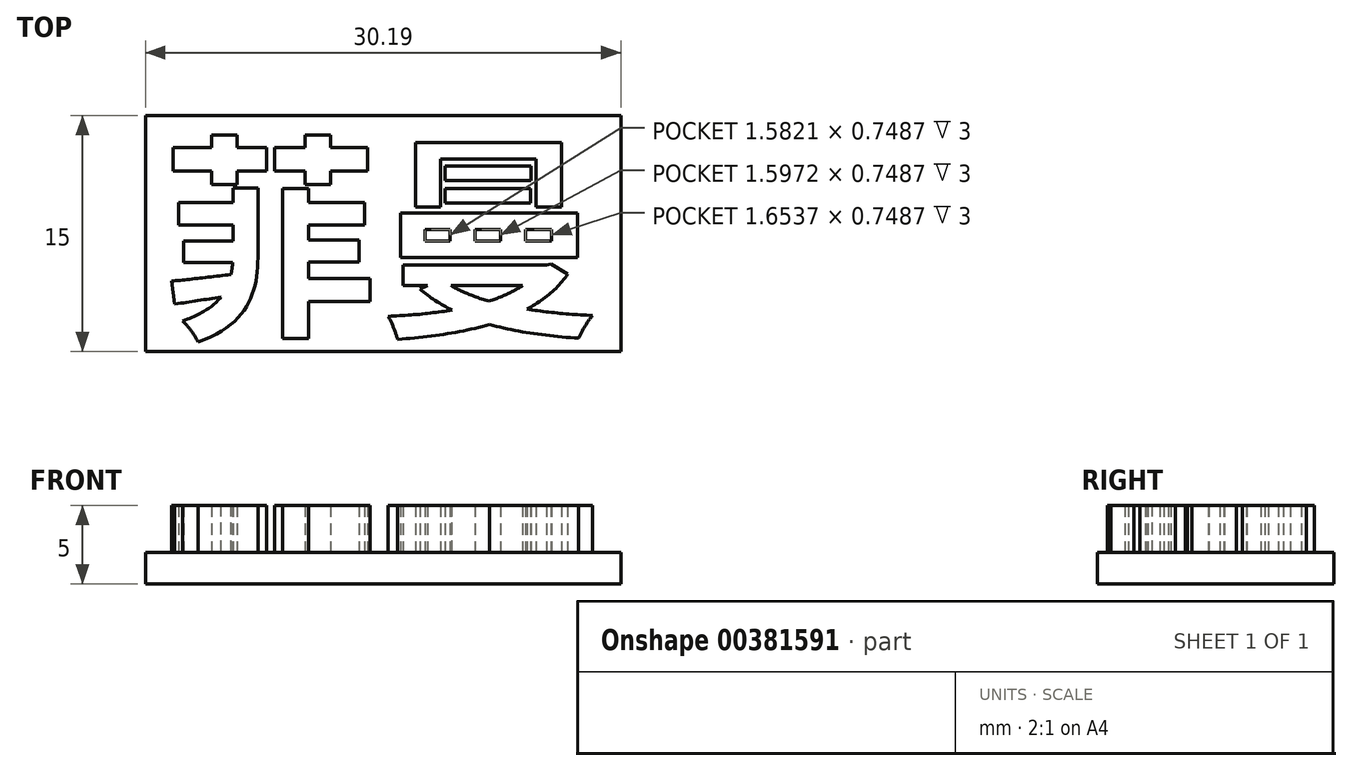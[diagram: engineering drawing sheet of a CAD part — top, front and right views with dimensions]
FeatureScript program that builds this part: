
annotation { "Feature Type Name" : "Feature", "Feature Type Description" : "" }
export const myFeature = defineFeature(function(context is Context, id is Id, definition is map)
    precondition{}
    {
        {
            var Q0;
            Q0=qCreatedBy(makeId("Top.planeOp"),FACE);
            var sketch = newSketch(context, id + "F0", { "sketchPlane" : qUnion([Q0])});
            skText(sketch, "E0", { "text": "菲曼", "fontName": "NotoSansCJKtc-Bold.otf"});
            skLineSegment(sketch, "E1.bottom", {"start": v(-1, 13) * mm, "end": v(29.2, 13) * mm});
            skLineSegment(sketch, "E1.top", {"start": v(-1, -2) * mm, "end": v(29.2, -2) * mm});
            skLineSegment(sketch, "E1.left", {"start": v(-1, 13) * mm, "end": v(-1, -2) * mm});
            skLineSegment(sketch, "E1.right", {"start": v(29.2, 13) * mm, "end": v(29.2, -2) * mm});
            const initialGuessF0  = {"E0": [0, 0, 1, 0, 0.01]};
            skSetInitialGuess(sketch, initialGuessF0);
            skSolve(sketch);
        }
        {
            var Q0;
            Q0=makeQuery(id+"F0.imprint","IMPRINT",FACE,{"disambiguationData":[TD([[makeQuery(id+"F0.imprint","IMPRINT",EDGE,{"derivedFrom":sQuery(id+"F0.wireOp",EDGE,"E0.sketch_text.stroke-0")}),-1.0]])]});
            var Q1;
            Q1=makeQuery(id+"F0.imprint","IMPRINT",FACE,{"disambiguationData":[TD([[makeQuery(id+"F0.imprint","IMPRINT",EDGE,{"derivedFrom":sQuery(id+"F0.wireOp",EDGE,"E0.sketch_text.stroke-0")}),1.0]])]});
            var Q2;
            Q2=makeQuery(id+"F0.imprint","IMPRINT",FACE,{"disambiguationData":[TD([[makeQuery(id+"F0.imprint","IMPRINT",EDGE,{"derivedFrom":sQuery(id+"F0.wireOp",EDGE,"E0.sketch_text.stroke-19")}),1.0]])]});
            var Q3;
            Q3=makeQuery(id+"F0.imprint","IMPRINT",FACE,{"disambiguationData":[TD([[makeQuery(id+"F0.imprint","IMPRINT",EDGE,{"derivedFrom":sQuery(id+"F0.wireOp",EDGE,"E0.sketch_text.stroke-45")}),1.0]])]});
            var Q4;
            Q4=makeQuery(id+"F0.imprint","IMPRINT",FACE,{"disambiguationData":[TD([[makeQuery(id+"F0.imprint","IMPRINT",EDGE,{"derivedFrom":sQuery(id+"F0.wireOp",EDGE,"E0.sketch_text.stroke-41")}),1.0]])]});
            var Q5;
            Q5=makeQuery(id+"F0.imprint","IMPRINT",FACE,{"disambiguationData":[TD([[makeQuery(id+"F0.imprint","IMPRINT",EDGE,{"derivedFrom":sQuery(id+"F0.wireOp",EDGE,"E0.sketch_text.stroke-37")}),1.0]])]});
            var Q6;
            Q6=makeQuery(id+"F0.imprint","IMPRINT",FACE,{"disambiguationData":[TD([[makeQuery(id+"F0.imprint","IMPRINT",EDGE,{"derivedFrom":sQuery(id+"F0.wireOp",EDGE,"E0.sketch_text.stroke-69")}),1.0]])]});
            var Q7;
            Q7=makeQuery(id+"F0.imprint","IMPRINT",FACE,{"disambiguationData":[TD([[makeQuery(id+"F0.imprint","IMPRINT",EDGE,{"derivedFrom":sQuery(id+"F0.wireOp",EDGE,"E0.sketch_text.stroke-69")}),-1.0]])]});
            var Q8;
            Q8=makeQuery(id+"F0.imprint","IMPRINT",FACE,{"disambiguationData":[TD([[makeQuery(id+"F0.imprint","IMPRINT",EDGE,{"derivedFrom":sQuery(id+"F0.wireOp",EDGE,"E0.sketch_text.stroke-49")}),1.0]])]});
            var Q9;
            Q9=makeQuery(id+"F0.imprint","IMPRINT",FACE,{"disambiguationData":[TD([[makeQuery(id+"F0.imprint","IMPRINT",EDGE,{"derivedFrom":sQuery(id+"F0.wireOp",EDGE,"E0.sketch_text.stroke-85")}),1.0]])]});
            var Q10;
            Q10=makeQuery(id+"F0.imprint","IMPRINT",FACE,{"disambiguationData":[TD([[makeQuery(id+"F0.imprint","IMPRINT",EDGE,{"derivedFrom":sQuery(id+"F0.wireOp",EDGE,"E0.sketch_text.stroke-85")}),-1.0]])]});
            var Q11;
            Q11=makeQuery(id+"F0.imprint","IMPRINT",FACE,{"disambiguationData":[TD([[makeQuery(id+"F0.imprint","IMPRINT",EDGE,{"derivedFrom":sQuery(id+"F0.wireOp",EDGE,"E0.sketch_text.stroke-138")}),1.0]])]});
            var Q12;
            Q12=makeQuery(id+"F0.imprint","IMPRINT",FACE,{"disambiguationData":[TD([[makeQuery(id+"F0.imprint","IMPRINT",EDGE,{"derivedFrom":sQuery(id+"F0.wireOp",EDGE,"E0.sketch_text.stroke-142")}),1.0]])]});
            var Q13;
            Q13=makeQuery(id+"F0.imprint","IMPRINT",FACE,{"disambiguationData":[TD([[makeQuery(id+"F0.imprint","IMPRINT",EDGE,{"derivedFrom":sQuery(id+"F0.wireOp",EDGE,"E0.sketch_text.stroke-57")}),1.0]])]});
            var Q14;
            Q14=makeQuery(id+"F0.imprint","IMPRINT",FACE,{"disambiguationData":[TD([[makeQuery(id+"F0.imprint","IMPRINT",EDGE,{"derivedFrom":sQuery(id+"F0.wireOp",EDGE,"E0.sketch_text.stroke-65")}),1.0]])]});
            var Q15;
            Q15=makeQuery(id+"F0.imprint","IMPRINT",FACE,{"disambiguationData":[TD([[makeQuery(id+"F0.imprint","IMPRINT",EDGE,{"derivedFrom":sQuery(id+"F0.wireOp",EDGE,"E0.sketch_text.stroke-81")}),-1.0]])]});
            var Q16;
            Q16=makeQuery(id+"F0.imprint","IMPRINT",FACE,{"disambiguationData":[TD([[makeQuery(id+"F0.imprint","IMPRINT",EDGE,{"derivedFrom":sQuery(id+"F0.wireOp",EDGE,"E0.sketch_text.stroke-77")}),-1.0]])]});
            var Q17;
            Q17=makeQuery(id+"F0.imprint","IMPRINT",FACE,{"disambiguationData":[TD([[makeQuery(id+"F0.imprint","IMPRINT",EDGE,{"derivedFrom":sQuery(id+"F0.wireOp",EDGE,"E0.sketch_text.stroke-73")}),-1.0]])]});
            var Q18;
            Q18=makeQuery(id+"F0.imprint","IMPRINT",FACE,{"disambiguationData":[TD([[makeQuery(id+"F0.imprint","IMPRINT",EDGE,{"derivedFrom":sQuery(id+"F0.wireOp",EDGE,"E0.sketch_text.stroke-89")}),1.0]])]});
            var Q19;
            Q19=makeQuery(id+"F0.imprint","IMPRINT",FACE,{"disambiguationData":[TD([[makeQuery(id+"F0.imprint","IMPRINT",EDGE,{"derivedFrom":sQuery(id+"F0.wireOp",EDGE,"E0.sketch_text.stroke-89")}),-1.0]])]});
            extrude(context, id + "F1", {"entities" : qUnion([Q0, Q1, Q2, Q3, Q4, Q5, Q6, Q7, Q8, Q9, Q10, Q11, Q12, Q13, Q14, Q15, Q16, Q17, Q18, Q19]), "oppositeDirection" : true, "depth" : 2 * mm, "offsetDistance" : 25 * mm});
        }
        {
            var Q0;
            Q0=makeQuery(id+"F0.imprint","IMPRINT",FACE,{"disambiguationData":[TD([[makeQuery(id+"F0.imprint","IMPRINT",EDGE,{"derivedFrom":sQuery(id+"F0.wireOp",EDGE,"E0.sketch_text.stroke-0")}),1.0]])]});
            var Q1;
            Q1=makeQuery(id+"F0.imprint","IMPRINT",FACE,{"disambiguationData":[TD([[makeQuery(id+"F0.imprint","IMPRINT",EDGE,{"derivedFrom":sQuery(id+"F0.wireOp",EDGE,"E0.sketch_text.stroke-19")}),1.0]])]});
            var Q2;
            Q2=makeQuery(id+"F0.imprint","IMPRINT",FACE,{"disambiguationData":[TD([[makeQuery(id+"F0.imprint","IMPRINT",EDGE,{"derivedFrom":sQuery(id+"F0.wireOp",EDGE,"E0.sketch_text.stroke-69")}),1.0]])]});
            var Q3;
            Q3=makeQuery(id+"F0.imprint","IMPRINT",FACE,{"disambiguationData":[TD([[makeQuery(id+"F0.imprint","IMPRINT",EDGE,{"derivedFrom":sQuery(id+"F0.wireOp",EDGE,"E0.sketch_text.stroke-37")}),1.0]])]});
            var Q4;
            Q4=makeQuery(id+"F0.imprint","IMPRINT",FACE,{"disambiguationData":[TD([[makeQuery(id+"F0.imprint","IMPRINT",EDGE,{"derivedFrom":sQuery(id+"F0.wireOp",EDGE,"E0.sketch_text.stroke-41")}),1.0]])]});
            var Q5;
            Q5=makeQuery(id+"F0.imprint","IMPRINT",FACE,{"disambiguationData":[TD([[makeQuery(id+"F0.imprint","IMPRINT",EDGE,{"derivedFrom":sQuery(id+"F0.wireOp",EDGE,"E0.sketch_text.stroke-45")}),1.0]])]});
            var Q6;
            Q6=makeQuery(id+"F0.imprint","IMPRINT",FACE,{"disambiguationData":[TD([[makeQuery(id+"F0.imprint","IMPRINT",EDGE,{"derivedFrom":sQuery(id+"F0.wireOp",EDGE,"E0.sketch_text.stroke-49")}),1.0]])]});
            var Q7;
            Q7=makeQuery(id+"F0.imprint","IMPRINT",FACE,{"disambiguationData":[TD([[makeQuery(id+"F0.imprint","IMPRINT",EDGE,{"derivedFrom":sQuery(id+"F0.wireOp",EDGE,"E0.sketch_text.stroke-138")}),1.0]])]});
            var Q8;
            Q8=makeQuery(id+"F0.imprint","IMPRINT",FACE,{"disambiguationData":[TD([[makeQuery(id+"F0.imprint","IMPRINT",EDGE,{"derivedFrom":sQuery(id+"F0.wireOp",EDGE,"E0.sketch_text.stroke-85")}),1.0]])]});
            var Q9;
            Q9=makeQuery(id+"F0.imprint","IMPRINT",FACE,{"disambiguationData":[TD([[makeQuery(id+"F0.imprint","IMPRINT",EDGE,{"derivedFrom":sQuery(id+"F0.wireOp",EDGE,"E0.sketch_text.stroke-142")}),1.0]])]});
            var Q10;
            Q10=makeQuery(id+"F0.imprint","IMPRINT",FACE,{"disambiguationData":[TD([[makeQuery(id+"F0.imprint","IMPRINT",EDGE,{"derivedFrom":sQuery(id+"F0.wireOp",EDGE,"E0.sketch_text.stroke-57")}),1.0]])]});
            var Q11;
            Q11=makeQuery(id+"F0.imprint","IMPRINT",FACE,{"disambiguationData":[TD([[makeQuery(id+"F0.imprint","IMPRINT",EDGE,{"derivedFrom":sQuery(id+"F0.wireOp",EDGE,"E0.sketch_text.stroke-65")}),1.0]])]});
            var Q12;
            Q12=makeQuery(id+"F0.imprint","IMPRINT",FACE,{"disambiguationData":[TD([[makeQuery(id+"F0.imprint","IMPRINT",EDGE,{"derivedFrom":sQuery(id+"F0.wireOp",EDGE,"E0.sketch_text.stroke-89")}),1.0]])]});
            extrude(context, id + "F2", {"entities" : qUnion([Q0, Q1, Q2, Q3, Q4, Q5, Q6, Q7, Q8, Q9, Q10, Q11, Q12]), "operationType" : NewBodyOperationType.ADD, "depth" : 3 * mm, "offsetDistance" : 25 * mm});
        }
    });
